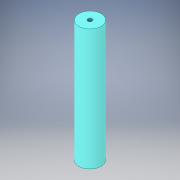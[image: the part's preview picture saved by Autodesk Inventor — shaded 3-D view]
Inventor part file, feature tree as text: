
AUTODESK INVENTOR PART (.ipt)
format: ipt  version: 2018 (Build 220112000, 112)  size: 115,712 bytes
history: native  units: in
note: dims shown in document units (in); Inventor stores cm internally (conversion verified against a paired STEP export)
features: sketch x3, hole x2, extrude x1
ambient origin geometry x8: Origin, YZ Plane, XZ Plane, XY Plane, X Axis, Y Axis, Z Axis, Center Point
bodies: Solid1 (feature_tree)
feature tree (6):
  extrude  "Extrusion1"  Depth=5.479in TaperAngle=0.0deg
  sketch  "Sketch3"  dims[d4=0.196in d5=0.5in d6=0.375in d7=0.25in d8=0.5635in d9=0.75in d10=0.8108in d11=0.5in d12=0.196in d13=0.5in d14=0.375in d15=0.25in d16=0.5635in d17=0.75in d18=0.8108in]
  hole  "Hole1"  [1 undecoded]
  hole  "Hole2"  [1 undecoded]
  sketch  "Sketch1"  dims[d0=1.0in d1=5.479in d2=0.0in]
  sketch  "Sketch2"  dims[d3=0.25in]
note: 2 required parameter values undecoded (feature->parameter linkage not recoverable at this tier; creation-order binding heuristic only, values carry confidence <= 0.55)
